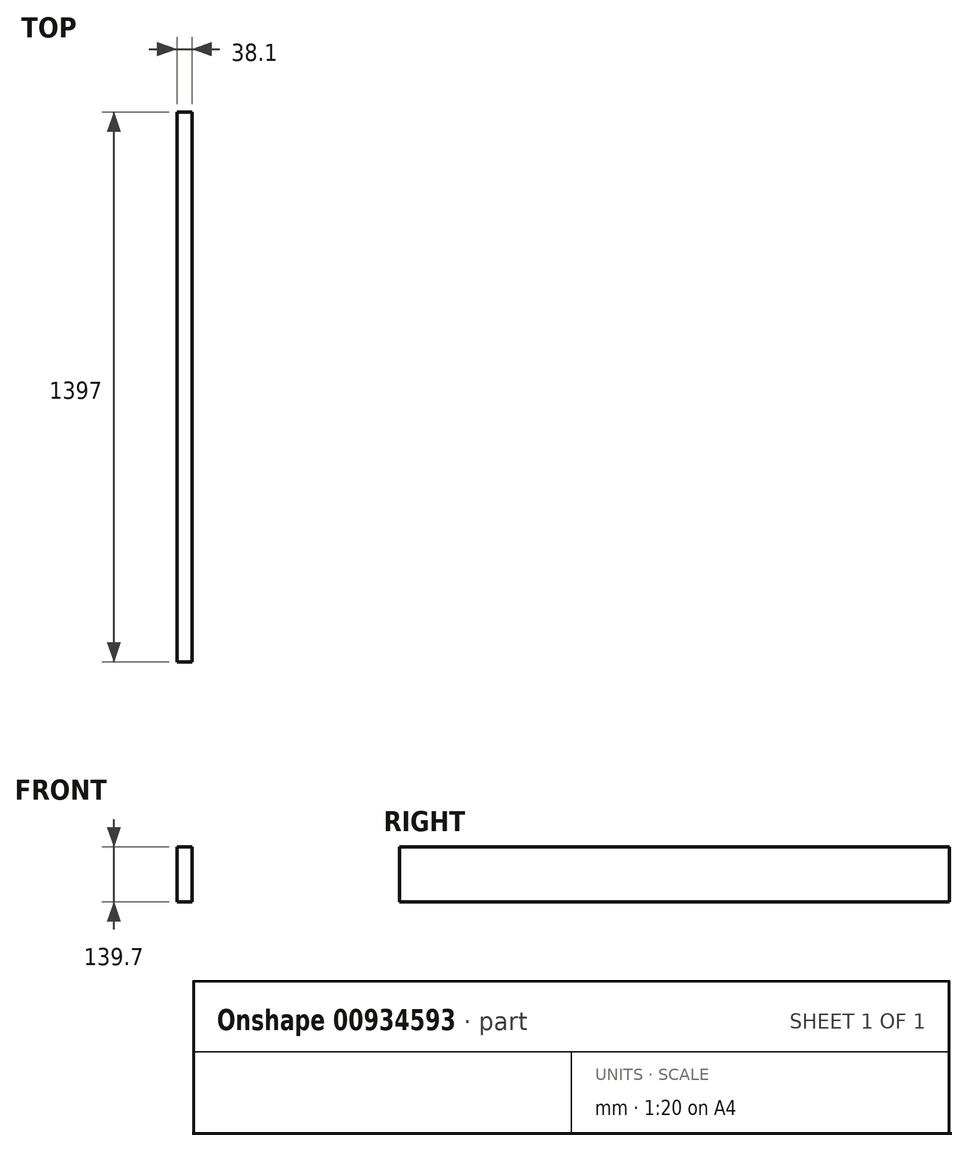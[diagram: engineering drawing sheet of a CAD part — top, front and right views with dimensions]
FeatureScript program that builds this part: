
annotation { "Feature Type Name" : "Feature", "Feature Type Description" : "" }
export const myFeature = defineFeature(function(context is Context, id is Id, definition is map)
    precondition{}
    {
        {
            var Q0;
            Q0=qCreatedBy(makeId("Front.planeOp"),FACE);
            var sketch = newSketch(context, id + "F0", { "sketchPlane" : qUnion([Q0])});
            skLineSegment(sketch, "E0.bottom", {"start": v(0, 0) * mm, "end": v(38.1, 0) * mm});
            skLineSegment(sketch, "E0.top", {"start": v(0, 139.7) * mm, "end": v(38.1, 139.7) * mm});
            skLineSegment(sketch, "E0.left", {"start": v(0, 0) * mm, "end": v(0, 139.7) * mm});
            skLineSegment(sketch, "E0.right", {"start": v(38.1, 0) * mm, "end": v(38.1, 139.7) * mm});
            skSolve(sketch);
        }
        {
            var Q0;
            Q0=makeQuery(id+"F0.imprint","IMPRINT",FACE,{"disambiguationData":[TD([[makeQuery(id+"F0.imprint","IMPRINT",EDGE,{"derivedFrom":sQuery(id+"F0.wireOp",EDGE,"E0.bottom")}),1.0]])]});
            extrude(context, id + "F1", {"entities" : qUnion([Q0]), "oppositeDirection" : true, "depth" : 1397 * mm, "offsetDistance" : 25.4 * mm});
        }
    });
